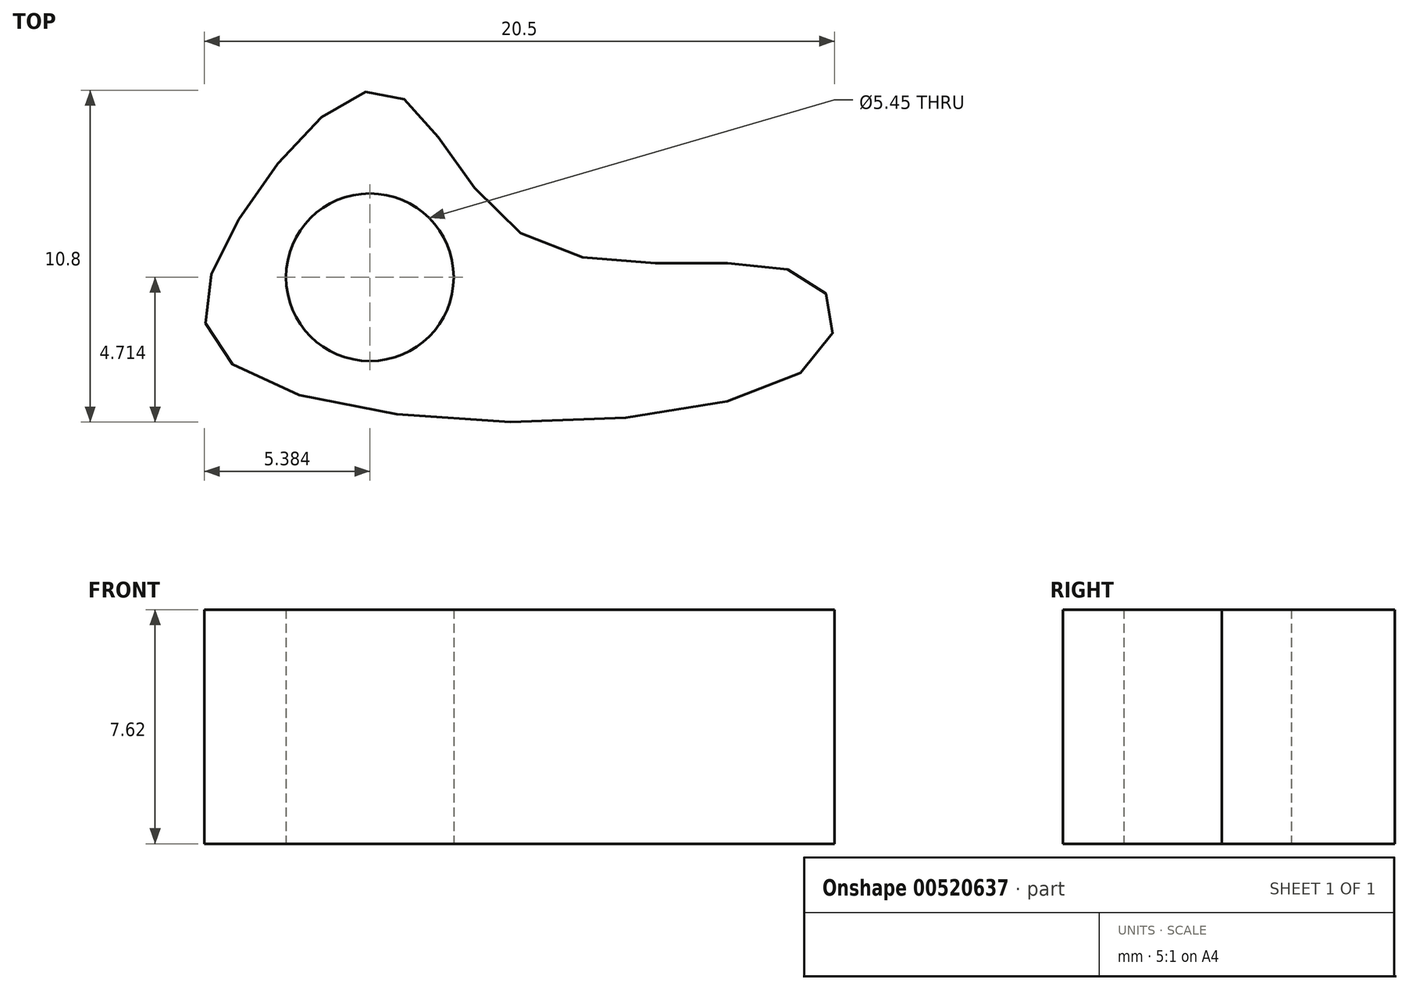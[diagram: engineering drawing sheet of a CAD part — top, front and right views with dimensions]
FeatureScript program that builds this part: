
annotation { "Feature Type Name" : "Feature", "Feature Type Description" : "" }
export const myFeature = defineFeature(function(context is Context, id is Id, definition is map)
    precondition{}
    {
        {
            var Q0;
            Q0=qCreatedBy(makeId("Top.planeOp"),FACE);
            var sketch = newSketch(context, id + "F0", { "sketchPlane" : qUnion([Q0])});
            skLineSegment(sketch, "E0.bottom", {"start": v(0, 0) * mm, "end": v(-76.82, 0) * mm});
            skLineSegment(sketch, "E0.top", {"start": v(0, 37.75) * mm, "end": v(-76.82, 37.75) * mm});
            skLineSegment(sketch, "E0.left", {"start": v(0, 0) * mm, "end": v(0, 37.75) * mm});
            skLineSegment(sketch, "E0.right", {"start": v(-76.82, 0) * mm, "end": v(-76.82, 37.75) * mm});
            skSolve(sketch);
        }
        {
            var Q0;
            Q0=makeQuery(id+"F0.imprint","IMPRINT",FACE,{"disambiguationData":[TD([[makeQuery(id+"F0.imprint","IMPRINT",EDGE,{"derivedFrom":sQuery(id+"F0.wireOp",EDGE,"E0.bottom")}),-1.0]])]});
            var sketch = newSketch(context, id + "F1", { "sketchPlane" : qUnion([Q0])});
            skFitSpline(sketch, "E1", {"points": [v(-18.52, 4.82) * mm, v(-13.67, 8.99) * mm, v(-8.97, 4.14) * mm, v(0, 2.92) * mm, v(0, 0) * mm, v(-18.6, 0) * mm, v(-18.52, 4.82) * mm]});
            skCircle(sketch, "E2", {"center": v(-14.26, 2.93) * mm, "radius": 2.73 * mm});
            skSolve(sketch);
        }
        {
            var Q0;
            Q0 = qSketchRegion(id + "F1", true);
            extrude(context, id + "F2", {"entities" : qUnion([Q0]), "depth" : 7.62 * mm, "offsetDistance" : 25.4 * mm});
        }
    });
